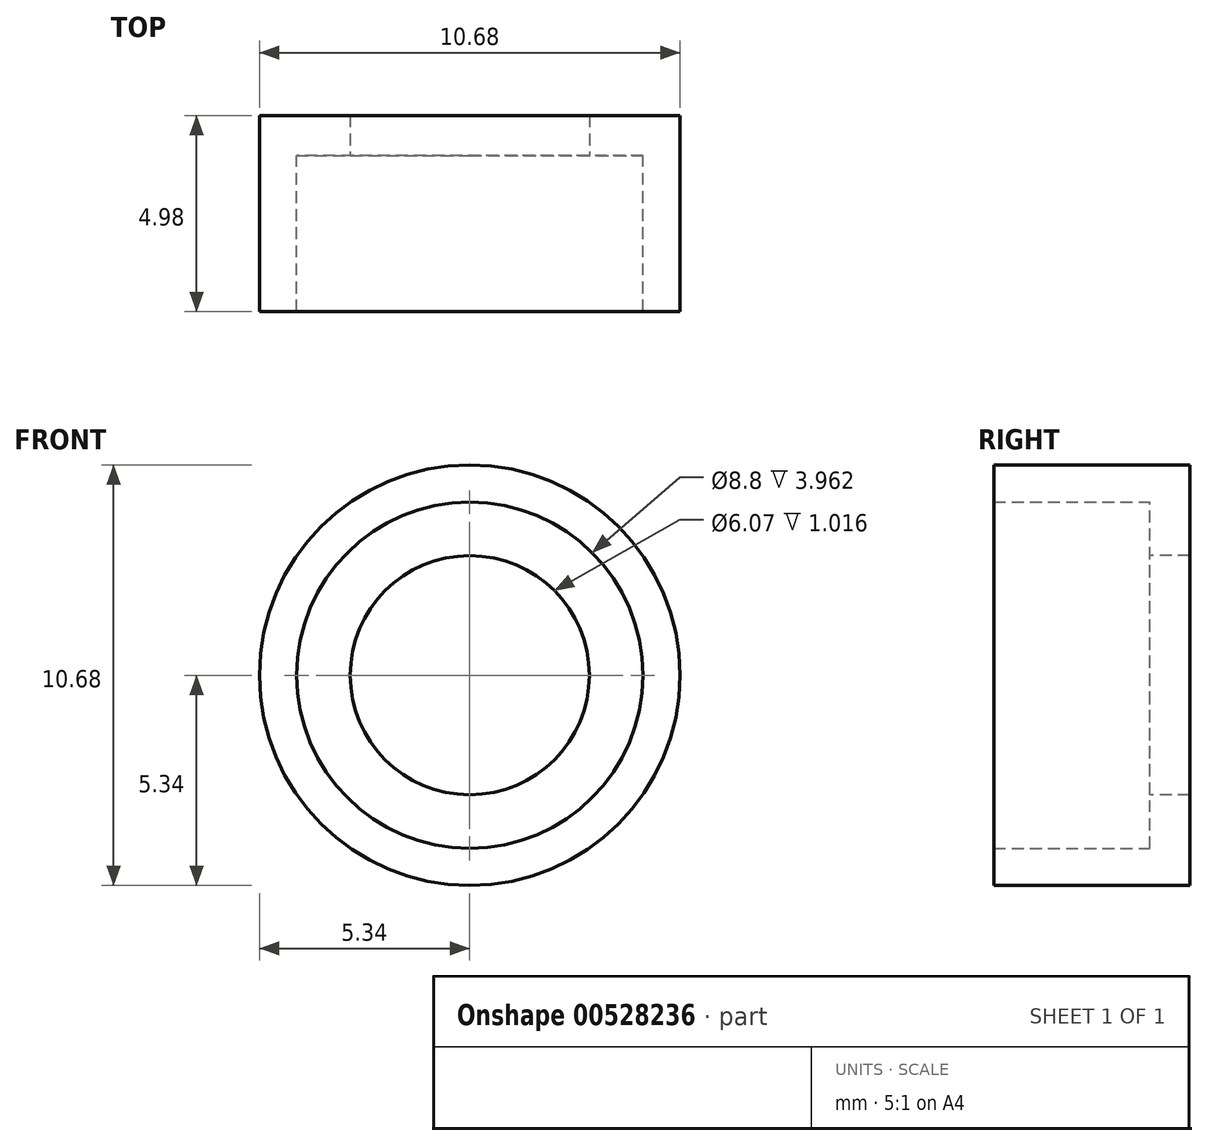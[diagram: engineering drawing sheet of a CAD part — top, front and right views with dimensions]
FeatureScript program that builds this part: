
annotation { "Feature Type Name" : "Feature", "Feature Type Description" : "" }
export const myFeature = defineFeature(function(context is Context, id is Id, definition is map)
    precondition{}
    {
        {
            var Q0;
            Q0=qCreatedBy(makeId("Front.planeOp"),FACE);
            var sketch = newSketch(context, id + "F0", { "sketchPlane" : qUnion([Q0])});
            skCircle(sketch, "E0", {"center": v(0, 0) * mm, "radius": 4.4 * mm});
            skCircle(sketch, "E1", {"center": v(0, 0) * mm, "radius": 5.34 * mm});
            skSolve(sketch);
        }
        {
            var Q0;
            Q0=makeQuery(id+"F0.imprint","IMPRINT",FACE,{"disambiguationData":[TD([[makeQuery(id+"F0.imprint","IMPRINT",EDGE,{"derivedFrom":sQuery(id+"F0.wireOp",EDGE,"E0")}),-1.0]])]});
            extrude(context, id + "F1", {"entities" : qUnion([Q0]), "depth" : 4.98 * mm, "offsetDistance" : 25.4 * mm});
        }
        {
            var Q0;
            Q0=qCreatedBy(makeId("Front.planeOp"),FACE);
            var sketch = newSketch(context, id + "F2", { "sketchPlane" : qUnion([Q0])});
            skCircle(sketch, "E2", {"center": v(0, 0) * mm, "radius": 4.62 * mm});
            skSolve(sketch);
        }
        {
            var Q0;
            Q0=makeQuery(id+"F2.imprint","IMPRINT",FACE,{"disambiguationData":[TD([[makeQuery(id+"F2.imprint","IMPRINT",EDGE,{"derivedFrom":sQuery(id+"F2.wireOp",EDGE,"E2")}),1.0]])]});
            extrude(context, id + "F3", {"entities" : qUnion([Q0]), "operationType" : NewBodyOperationType.ADD, "depth" : 1.02 * mm, "offsetDistance" : 25.4 * mm});
        }
        {
            var Q0;
            Q0=qCreatedBy(makeId("Front.planeOp"),FACE);
            var sketch = newSketch(context, id + "F4", { "sketchPlane" : qUnion([Q0])});
            skCircle(sketch, "E3", {"center": v(0, 0) * mm, "radius": 3.04 * mm});
            skSolve(sketch);
        }
        {
            var Q0;
            Q0=makeQuery(id+"F4.imprint","IMPRINT",FACE,{"disambiguationData":[TD([[makeQuery(id+"F4.imprint","IMPRINT",EDGE,{"derivedFrom":sQuery(id+"F4.wireOp",EDGE,"E3")}),1.0]])]});
            extrude(context, id + "F5", {"entities" : qUnion([Q0]), "operationType" : NewBodyOperationType.REMOVE, "oppositeDirection" : true, "depth" : 25.4 * mm, "offsetDistance" : 25.4 * mm, "hasSecondDirection" : true, "secondDirectionOppositeDirection" : false, "secondDirectionDepth" : 25.4 * mm});
        }
    });
